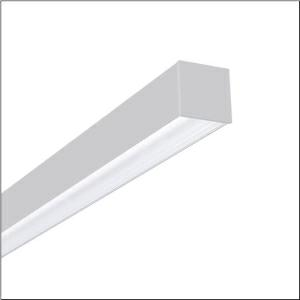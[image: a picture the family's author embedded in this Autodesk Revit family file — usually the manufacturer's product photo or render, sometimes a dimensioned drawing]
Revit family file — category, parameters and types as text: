
# Revit family: silica_r_5mx21dd1w4a_969a
name_source: partatom
category: Lighting Fixtures
units: mm (PartAtom-declared; Revit-internal decimal feet)

## family parameters
Cut with Voids When Loaded = No
Host = Face
Light Source = No
Part Type = Normal
Room Calculation Point = No
Round Connector Dimension = Use Diameter
Shared = No

## types (1)
- --- (1 x LED, 3140 lm, 22.6 W, 4000K)
    Apparent Load = 23 VA
    CIE Flux Codes = 47 79 96 100 100
    Color Rendering = 80
    Color Temperature = 4000K
    Default Elevation = 1800 mm
    Description = Silica®, office luminaire, of aluminium, opal, light emission: direct distribution, primary light characteristic: symmetric, installation type: surface-mounted, LED, rated luminous flux: 3.010lm, luminous efficacy: 123lm/W, light colour: 840, colour temperature: 4000K, control gear: ECG DALI, with terminal, 3+2-pole, max. 2.5mm², mains connection: 230V, AC, 50/60Hz, rated input power: 24W, luminaire housing, of aluminium, traffic white (RAL 9016), length: 1.442mm, width: 65mm, height: 64mm, protection rating (complete): IP20, insulation class (complete): insulation class I (protective earthing), certification: CE, permissible operating ambient temperature: 0..+35°C, standard: EN 50419, packaging unit: 1 piece
    Height = 64 mm
    Lamp = 1 x LED
    Lamp Light Flux = 3140 lm
    Lamp Power = 22.6 W
    Lamp count = 1
    Length = 1442 mm
    Luminous efficacy = 139 lm/W
    Manufacturer = Siteco
    ModVariant = No
    Model = 5MX21DD1W4A
    Mounting Place = Ceiling
    Mounting Type = Surface mounted
    Number of Poles = 1
    OnlyDefault = Yes
    Power Factor = 1
    Product Name = Silica®
    Product group = office luminaire | ceiling mounted
    ProductGroupID = 304
    Protection Class = Protection class I
    Protection Degree = IP 20
    RLX_Detail_Level = 1
    RLX_Emergency_Light_Flux = 0 lm
    RLX_Emergency_Type = 0
    RLX_Emergency_Type_DB = No
    RlxData = <blob elided: 22737 chars, md5=12082132>
    Socket = socket
    Standby Power = 0 W
    System Light Flux = 3140 lm
    System Power = 23 W
    Type Comments = factory setting: luminous flux: 100 % | dim-lin: 254 | 125 mA
    Type Image = l_248206.jpg
    URL = http://relux.com
    VarID = @adj_171801
    Voltage = 0 V
    Weight = 0.00 kg
    Width = 65 mm

## geometry (parser evidence)
native form markers: Blend x4, Sweep x12
no freeform markers — native parametric forms only
